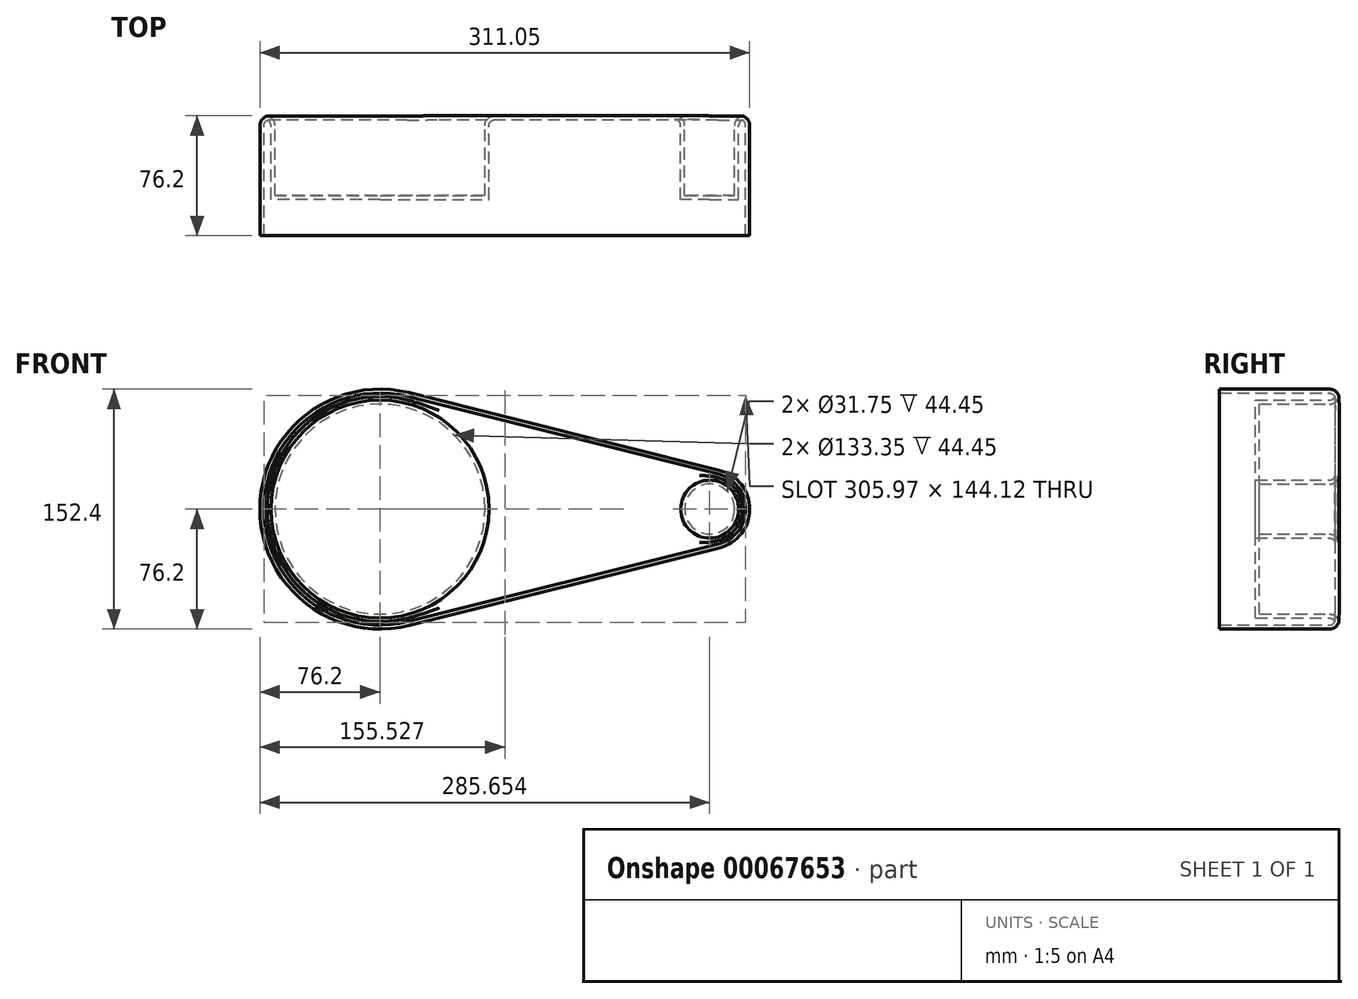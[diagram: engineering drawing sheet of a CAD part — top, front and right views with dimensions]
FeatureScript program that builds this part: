
annotation { "Feature Type Name" : "Feature", "Feature Type Description" : "" }
export const myFeature = defineFeature(function(context is Context, id is Id, definition is map)
    precondition{}
    {
        {
            var Q0;
            Q0=qCreatedBy(makeId("Front.planeOp"),FACE);
            var sketch = newSketch(context, id + "F0", { "sketchPlane" : qUnion([Q0])});
            skCircle(sketch, "E0", {"center": v(0, 0) * mm, "radius": 76.2 * mm});
            skCircle(sketch, "E1", {"center": v(209.45, 0) * mm, "radius": 25.4 * mm});
            skLineSegment(sketch, "E2", {"start": v(18.48, 73.92) * mm, "end": v(215.61, 24.64) * mm});
            skLineSegment(sketch, "E3", {"start": v(18.48, -73.92) * mm, "end": v(215.61, -24.64) * mm});
            skSolve(sketch);
        }
        {
            var Q0;
            {var subQ0=sQuery(id+"F0.wireOp",EDGE,"E0");var subQ1=makeQuery(id+"F0.imprint","INTERSECT",VERTEX,{"derivedFrom":[subQ0,sQuery(id+"F0.wireOp",EDGE,"E2")]});Q0=makeQuery(id+"F0.imprint","IMPRINT",FACE,{"disambiguationData":[TD([[makeQuery(id+"F0.imprint","IMPRINT",EDGE,{"disambiguationData":[TD([[subQ1,-1.0]])],"derivedFrom":subQ0}),1.0]])]});}
            var Q1;
            {var subQ0=sQuery(id+"F0.wireOp",EDGE,"E2");Q1=makeQuery(id+"F0.imprint","IMPRINT",FACE,{"disambiguationData":[TD([[makeQuery(id+"F0.imprint","IMPRINT",EDGE,{"derivedFrom":subQ0}),-1.0]])]});}
            var Q2;
            {var subQ0=sQuery(id+"F0.wireOp",EDGE,"E1");var subQ1=makeQuery(id+"F0.imprint","INTERSECT",VERTEX,{"derivedFrom":[subQ0,sQuery(id+"F0.wireOp",EDGE,"E2")]});Q2=makeQuery(id+"F0.imprint","IMPRINT",FACE,{"disambiguationData":[TD([[makeQuery(id+"F0.imprint","IMPRINT",EDGE,{"disambiguationData":[TD([[subQ1,-1.0]])],"derivedFrom":subQ0}),1.0]])]});}
            extrude(context, id + "F1", {"entities" : qUnion([Q0, Q1, Q2]), "depth" : 76.2 * mm});
        }
        {
            var Q0;
            {var subQ0=sQuery(id+"F0.wireOp",EDGE,"E2");Q0=makeQuery(id+"F0.imprint","IMPRINT",FACE,{"disambiguationData":[TD([[makeQuery(id+"F0.imprint","IMPRINT",EDGE,{"derivedFrom":subQ0}),-1.0]])]});}
            var sketch = newSketch(context, id + "F2", { "sketchPlane" : qUnion([Q0])});
            skCircle(sketch, "E4", {"center": v(0, 0) * mm, "radius": 66.68 * mm});
            skCircle(sketch, "E5", {"center": v(209.45, 0) * mm, "radius": 15.88 * mm});
            skSolve(sketch);
        }
        {
            var Q0;
            Q0=makeQuery(id+"F2.imprint","IMPRINT",FACE,{"disambiguationData":[TD([[makeQuery(id+"F2.imprint","IMPRINT",EDGE,{"derivedFrom":sQuery(id+"F2.wireOp",EDGE,"E4")}),1.0]])]});
            var Q1;
            Q1=makeQuery(id+"F2.imprint","IMPRINT",FACE,{"disambiguationData":[TD([[makeQuery(id+"F2.imprint","IMPRINT",EDGE,{"derivedFrom":sQuery(id+"F2.wireOp",EDGE,"E5")}),1.0]])]});
            extrude(context, id + "F3", {"entities" : qUnion([Q0, Q1]), "operationType" : NewBodyOperationType.REMOVE, "depth" : 50.8 * mm});
        }
        {
            var Q0;
            Q0=makeQuery(id+"F1.opExtrude","CAP_FACE",FACE,{"disambiguationData":[OSD([sQuery(id+"F0.wireOp",EDGE,"E0"),sQuery(id+"F0.wireOp",EDGE,"E1"),sQuery(id+"F0.wireOp",EDGE,"E2"),sQuery(id+"F0.wireOp",EDGE,"E3")])],"isStart":true});
            fillet(context, id + "F4", {"entities" : qUnion([Q0]), "radius" : 6.35 * mm, "tangentPropagation" : true, "allowEdgeOverflow" : false});
        }
        {
            var Q0;
            Q0=makeQuery(id+"F1.opExtrude","CAP_FACE",FACE,{"disambiguationData":[OSD([sQuery(id+"F0.wireOp",EDGE,"E0"),sQuery(id+"F0.wireOp",EDGE,"E1"),sQuery(id+"F0.wireOp",EDGE,"E2"),sQuery(id+"F0.wireOp",EDGE,"E3")])],"isStart":false});
            shell(context, id + "F5", {"entities" : qUnion([Q0]), "thickness" : 2.54 * mm});
        }
    });
